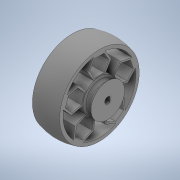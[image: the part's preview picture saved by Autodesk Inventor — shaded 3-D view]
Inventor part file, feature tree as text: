
AUTODESK INVENTOR PART (.ipt)
format: ipt  version: 2020 (Build 240168000, 168)  size: 419,328 bytes
history: native  units: in
note: dims shown in document units (in); Inventor stores cm internally (conversion verified against a paired STEP export)
features: sketch x4, extrude x2, revolve x2, projected_geometry x1
ambient origin geometry x8: Origin, YZ Plane, XZ Plane, XY Plane, X Axis, Y Axis, Z Axis, Center Point
bodies: Solid1 (feature_tree)
feature tree (9):
  extrude  "Extrusion1"  Depth=0.0394in
  sketch  "Sketch3"  dims[d6=0.6299in d7=0.1575in]
  revolve  "Revolution1"  [1 undecoded]
  extrude  "Extrusion2"  Depth=0.1575in
  revolve  "Revolution2"  [1 undecoded]
  sketch  "Sketch1"  dims[d0=0.1181in d1=0.0394in]
  sketch  "Sketch2"  dims[d3=1.4961in d4=0.1181in]
  projected_geometry  "Projected Loop1"
  sketch  "Sketch4"  dims[d8=0.0in d9=1.4961in d10=0.063in d11=0.0315in d16=0.5118in d17=0.0in d19=360.0deg d20=0.0787in d24=0.0394in d25=90.0deg d26=45.0deg d28=0.0079in d29=1.9685in d31=360.0deg]
note: 2 required parameter values undecoded (feature->parameter linkage not recoverable at this tier; creation-order binding heuristic only, values carry confidence <= 0.55)
